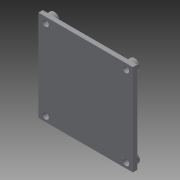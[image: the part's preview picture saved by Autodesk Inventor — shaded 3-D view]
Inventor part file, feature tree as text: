
AUTODESK INVENTOR PART (.ipt)
format: ipt  version: 2013 (Build 170138000, 138)  size: 104,960 bytes
history: native  units: mm
features: extrude x2, sketch x2
ambient origin geometry x8: Origin, YZ Plane, XZ Plane, XY Plane, X Axis, Y Axis, Z Axis, Center Point
bodies: Solid1 (feature_tree)
feature tree (4):
  extrude  "Extrusion1"  Depth=42.0mm
  extrude  "Extrusion2"  Depth=3.0mm
  sketch  "Sketch1"  dims[d0=43.5mm d2=42.0mm]
  sketch  "Sketch2"  dims[d3=3.0mm d4=3.0mm d7=3.25mm d8=2.5mm d9=3.25mm d10=2.5mm d11=2.0mm d12=0.0mm d13=5.0mm d14=5.0mm d15=2.0mm d16=0.0mm]
